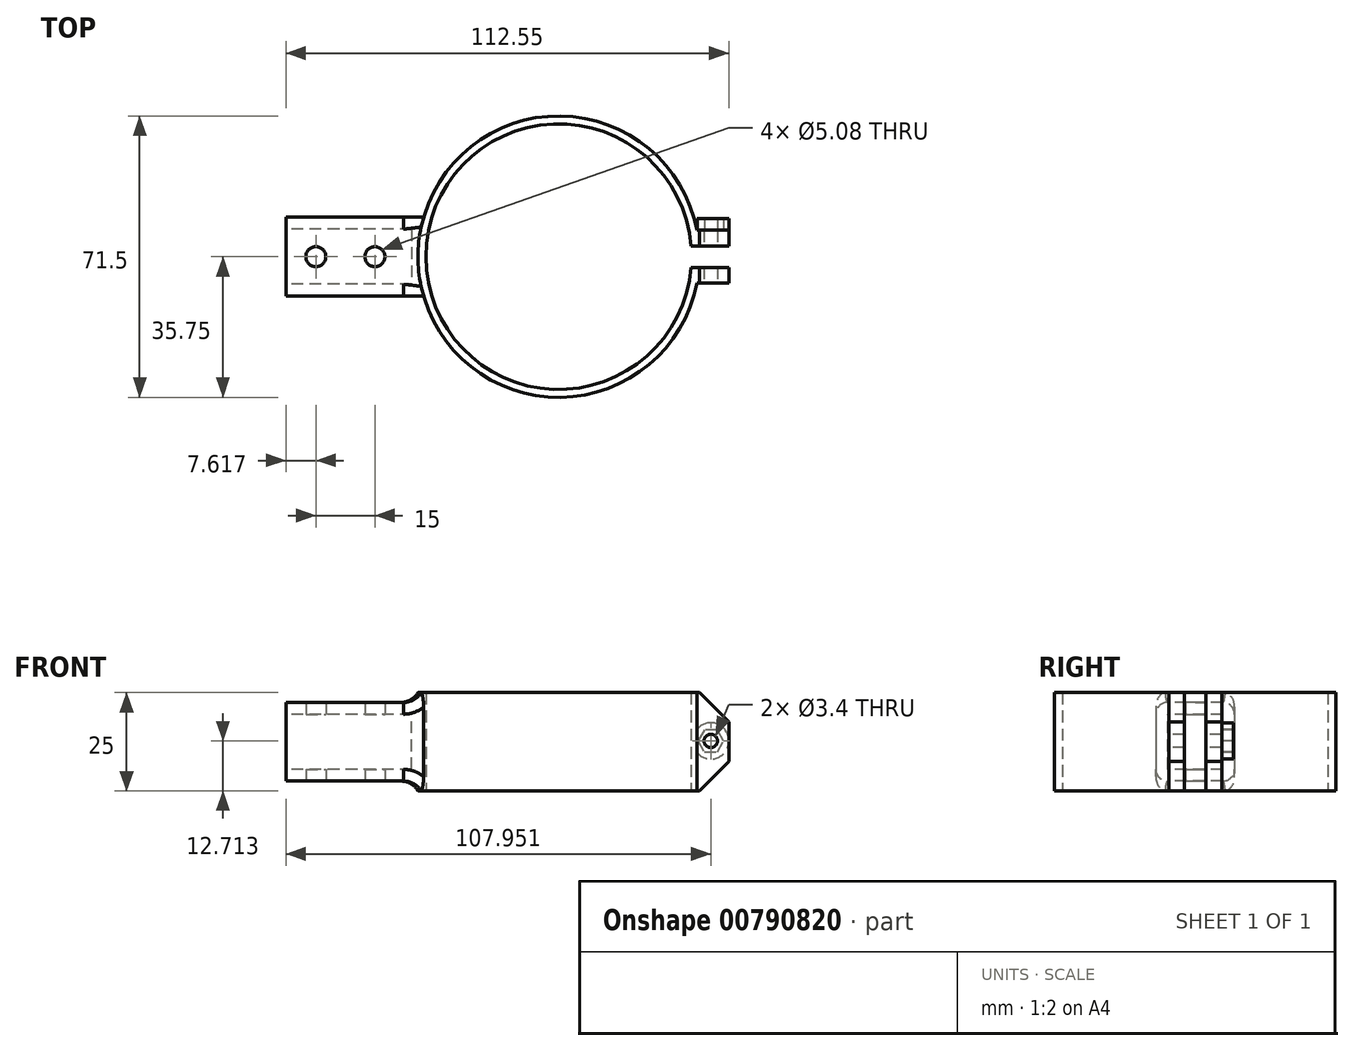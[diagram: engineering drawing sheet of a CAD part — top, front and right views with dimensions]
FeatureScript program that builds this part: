
annotation { "Feature Type Name" : "Feature", "Feature Type Description" : "" }
export const myFeature = defineFeature(function(context is Context, id is Id, definition is map)
    precondition{}
    {
        {
            var Q0;
            Q0=qCreatedBy(makeId("Top.planeOp"),FACE);
            var sketch = newSketch(context, id + "F0", { "sketchPlane" : qUnion([Q0])});
            skCircle(sketch, "E0", {"center": v(0, 0) * mm, "radius": 33.75 * mm});
            skCircle(sketch, "E1.0", {"center": v(0, 0) * mm, "radius": 35.75 * mm});
            skLineSegment(sketch, "E2.bottom", {"start": v(33.64, 6.72) * mm, "end": v(43.23, 6.72) * mm});
            skLineSegment(sketch, "E2.top", {"start": v(33.64, 2.72) * mm, "end": v(43.23, 2.72) * mm});
            skLineSegment(sketch, "E2.left", {"start": v(33.64, 6.72) * mm, "end": v(33.64, 2.72) * mm});
            skLineSegment(sketch, "E2.right", {"start": v(43.23, 6.72) * mm, "end": v(43.23, 2.72) * mm});
            skLineSegment(sketch, "E3.MirrorCS", {"start": v(33.64, -2.72) * mm, "end": v(43.23, -2.72) * mm});
            skLineSegment(sketch, "E4.MirrorCS", {"start": v(33.64, -6.72) * mm, "end": v(33.64, -2.72) * mm});
            skLineSegment(sketch, "E5.MirrorCS", {"start": v(43.23, -6.72) * mm, "end": v(43.23, -2.72) * mm});
            skLineSegment(sketch, "E6.MirrorCS", {"start": v(33.64, -6.72) * mm, "end": v(43.23, -6.72) * mm});
            skSolve(sketch);
        }
        {
            var Q0;
            {var subQ5=sQuery(id+"F0.wireOp",EDGE,"E2.right");Q0=makeQuery(id+"F0.imprint","IMPRINT",FACE,{"disambiguationData":[TD([[makeQuery(id+"F0.imprint","IMPRINT",EDGE,{"derivedFrom":subQ5}),-1.0]])]});}
            var Q1;
            {var subQ0=sQuery(id+"F0.wireOp",EDGE,"E2.left");Q1=makeQuery(id+"F0.imprint","IMPRINT",FACE,{"disambiguationData":[TD([[makeQuery(id+"F0.imprint","IMPRINT",EDGE,{"derivedFrom":subQ0}),-1.0]])]});}
            var Q2;
            {var subQ5=sQuery(id+"F0.wireOp",EDGE,"E2.left");Q2=makeQuery(id+"F0.imprint","IMPRINT",FACE,{"disambiguationData":[TD([[makeQuery(id+"F0.imprint","IMPRINT",EDGE,{"derivedFrom":subQ5}),1.0]])]});}
            var Q3;
            {var subQ5=sQuery(id+"F0.wireOp",EDGE,"E5.MirrorCS");Q3=makeQuery(id+"F0.imprint","IMPRINT",FACE,{"disambiguationData":[TD([[makeQuery(id+"F0.imprint","IMPRINT",EDGE,{"derivedFrom":subQ5}),1.0]])]});}
            var Q4;
            {var subQ5=sQuery(id+"F0.wireOp",EDGE,"E4.MirrorCS");Q4=makeQuery(id+"F0.imprint","IMPRINT",FACE,{"disambiguationData":[TD([[makeQuery(id+"F0.imprint","IMPRINT",EDGE,{"derivedFrom":subQ5}),-1.0]])]});}
            extrude(context, id + "F1", {"entities" : qUnion([Q0, Q1, Q2, Q3, Q4]), "depth" : 25 * mm, "offsetDistance" : 25 * mm});
        }
        {
            var Q0;
            Q0=makeQuery(id+"F1.opExtrude","CAP_EDGE",EDGE,{"disambiguationData":[OSD([sQuery(id+"F0.wireOp",EDGE,"E5.MirrorCS")])],"isStart":false});
            var Q1;
            Q1=makeQuery(id+"F1.opExtrude","CAP_EDGE",EDGE,{"disambiguationData":[OSD([sQuery(id+"F0.wireOp",EDGE,"E2.right")])],"isStart":false});
            var Q2;
            Q2=makeQuery(id+"F1.opExtrude","CAP_EDGE",EDGE,{"disambiguationData":[OSD([sQuery(id+"F0.wireOp",EDGE,"E5.MirrorCS")])],"isStart":true});
            var Q3;
            Q3=makeQuery(id+"F1.opExtrude","CAP_EDGE",EDGE,{"disambiguationData":[OSD([sQuery(id+"F0.wireOp",EDGE,"E2.right")])],"isStart":true});
            chamfer(context, id + "F2", {"entities" : qUnion([Q0, Q1, Q2, Q3]), "width" : 7.5 * mm, "tangentPropagation" : true});
        }
        {
            var Q0;
            Q0=makeQuery(id+"F1.opExtrude","SWEPT_FACE",FACE,{"disambiguationData":[OSD([sQuery(id+"F0.wireOp",EDGE,"E6.MirrorCS")])]});
            var sketch = newSketch(context, id + "F3", { "sketchPlane" : qUnion([Q0])});
            skCircle(sketch, "E7", {"center": v(38.63, 12.71) * mm, "radius": 1.7 * mm});
            skSolve(sketch);
        }
        {
            var Q0;
            Q0 = qSketchRegion(id + "F3", true);
            extrude(context, id + "F4", {"entities" : qUnion([Q0]), "operationType" : NewBodyOperationType.REMOVE, "oppositeDirection" : true, "depth" : 25 * mm, "offsetDistance" : 25 * mm});
        }
        {
            var Q0;
            Q0=makeQuery(id+"F1.opExtrude","SWEPT_FACE",FACE,{"disambiguationData":[OSD([sQuery(id+"F0.wireOp",EDGE,"E2.bottom")])]});
            var sketch = newSketch(context, id + "F5", { "sketchPlane" : qUnion([Q0])});
            skCircle(sketch, "E8.cCircle", {"center": v(-38.63, 12.71) * mm, "radius": 2.85 * mm, "construction": true});
            skLineSegment(sketch, "E8.0", {"start": v(-36.99, 9.86) * mm, "end": v(-40.28, 9.86) * mm});
            skLineSegment(sketch, "E8.1", {"start": v(-40.28, 9.86) * mm, "end": v(-41.92, 12.71) * mm});
            skLineSegment(sketch, "E8.2", {"start": v(-41.92, 12.71) * mm, "end": v(-40.28, 15.56) * mm});
            skLineSegment(sketch, "E8.3", {"start": v(-40.28, 15.56) * mm, "end": v(-36.99, 15.56) * mm});
            skLineSegment(sketch, "E8.4", {"start": v(-36.99, 15.56) * mm, "end": v(-35.34, 12.71) * mm});
            skLineSegment(sketch, "E8.5", {"start": v(-35.34, 12.71) * mm, "end": v(-36.99, 9.86) * mm});
            skPoint(sketch, "E8.0.midPoint", {"position": v(-38.63, 9.86) * mm});
            skCircle(sketch, "E9", {"center": v(-38.63, 12.71) * mm, "radius": 4.6 * mm});
            skSolve(sketch);
        }
        {
            var Q0;
            Q0=makeQuery(id+"F5.imprint","IMPRINT",FACE,{"disambiguationData":[TD([[makeQuery(id+"F5.imprint","IMPRINT",EDGE,{"derivedFrom":sQuery(id+"F5.wireOp",EDGE,"E8.0")}),1.0]])]});
            extrude(context, id + "F6", {"entities" : qUnion([Q0]), "operationType" : NewBodyOperationType.ADD, "depth" : 3 * mm, "offsetDistance" : 25 * mm});
        }
        {
            var Q0;
            Q0=qCreatedBy(makeId("Top.planeOp"),FACE);
            cPlane(context, id + "F7", {"entities" : qUnion([Q0]), "cplaneType" : CPlaneType.OFFSET, "offset" : 12.5 * mm, "width" : 150 * mm, "height" : 150 * mm});
        }
        {
            var Q0;
            Q0=qCreatedBy(id+"F7.planeOp",FACE);
            var sketch = newSketch(context, id + "F8", { "sketchPlane" : qUnion([Q0])});
            skLineSegment(sketch, "E10", {"start": v(-34.32, 10) * mm, "end": v(-69.32, 10) * mm});
            skLineSegment(sketch, "E11", {"start": v(-69.32, 10) * mm, "end": v(-69.32, -10) * mm});
            skLineSegment(sketch, "E12", {"start": v(-69.32, -10) * mm, "end": v(-34.32, -10) * mm});
            skLineSegment(sketch, "E13", {"start": v(-34.32, 10) * mm, "end": v(-33.75, 0) * mm});
            skLineSegment(sketch, "E14", {"start": v(-33.75, 0) * mm, "end": v(-34.32, -10) * mm});
            skSolve(sketch);
        }
        {
            var Q0;
            Q0 = qSketchRegion(id + "F8", true);
            extrude(context, id + "F9", {"entities" : qUnion([Q0]), "operationType" : NewBodyOperationType.ADD, "depth" : 10 * mm, "offsetDistance" : 25 * mm, "hasSecondDirection" : true, "secondDirectionOppositeDirection" : true, "secondDirectionDepth" : 10 * mm});
        }
        {
            var Q0;
            Q0=makeQuery(id+"F9.opExtrude","SWEPT_FACE",FACE,{"disambiguationData":[OSD([sQuery(id+"F8.wireOp",EDGE,"E11")])]});
            var sketch = newSketch(context, id + "F10", { "sketchPlane" : qUnion([Q0])});
            skSolve(sketch);
        }
        {
            var Q0;
            {var subQ0=sQuery(id+"F8.wireOp",EDGE,"E11");Q0=makeQuery(id+"F10.imprint","IMPRINT",FACE,{"disambiguationData":[TD([[makeQuery(id+"F10.imprint","IMPRINT",EDGE,{"derivedFrom":makeQuery(id+"F9.opExtrude","CAP_EDGE",EDGE,{"disambiguationData":[OSD([subQ0])],"isStart":true})}),1.0]])]});}
            var sketch = newSketch(context, id + "F11", { "sketchPlane" : qUnion([Q0])});
            skLineSegment(sketch, "E15.bottom", {"start": v(-7, 5.5) * mm, "end": v(7, 5.5) * mm});
            skLineSegment(sketch, "E15.top", {"start": v(-7, 19.5) * mm, "end": v(7, 19.5) * mm});
            skLineSegment(sketch, "E15.left", {"start": v(-7, 5.5) * mm, "end": v(-7, 19.5) * mm});
            skLineSegment(sketch, "E15.right", {"start": v(7, 5.5) * mm, "end": v(7, 19.5) * mm});
            skSolve(sketch);
        }
        {
            var Q0;
            Q0 = qSketchRegion(id + "F11", true);
            extrude(context, id + "F12", {"entities" : qUnion([Q0]), "operationType" : NewBodyOperationType.REMOVE, "oppositeDirection" : true, "depth" : 32 * mm, "offsetDistance" : 25 * mm});
        }
        {
            var Q0;
            Q0=makeQuery(id+"F9.opExtrude","CAP_FACE",FACE,{"disambiguationData":[OSD([sQuery(id+"F8.wireOp",EDGE,"E10"),sQuery(id+"F8.wireOp",EDGE,"E11"),sQuery(id+"F8.wireOp",EDGE,"E12"),sQuery(id+"F8.wireOp",EDGE,"E13"),sQuery(id+"F8.wireOp",EDGE,"E14")])],"isStart":true});
            var sketch = newSketch(context, id + "F13", { "sketchPlane" : qUnion([Q0])});
            skCircle(sketch, "E16", {"center": v(-61.7, 0) * mm, "radius": 2.54 * mm});
            skLineSegment(sketch, "E17", {"start": v(-61.7, 0) * mm, "end": v(-69.32, 0) * mm, "construction": true});
            skLineSegment(sketch, "E18", {"start": v(-61.7, 0) * mm, "end": v(-46.7, 0) * mm, "construction": true});
            skCircle(sketch, "E19", {"center": v(-46.7, 0) * mm, "radius": 2.54 * mm});
            skSolve(sketch);
        }
        {
            var Q0;
            Q0=makeQuery(id+"F13.imprint","IMPRINT",FACE,{"disambiguationData":[TD([[makeQuery(id+"F13.imprint","IMPRINT",EDGE,{"derivedFrom":sQuery(id+"F13.wireOp",EDGE,"E16")}),1.0]])]});
            extrude(context, id + "F14", {"entities" : qUnion([Q0]), "operationType" : NewBodyOperationType.REMOVE, "oppositeDirection" : true, "depth" : 25 * mm, "offsetDistance" : 25 * mm});
        }
        {
            var Q0;
            Q0=makeQuery(id+"F9.opExtrude","SWEPT_EDGE",EDGE,{"disambiguationData":[OSD([sQuery(id+"F8.wireOp",EDGE,"E12"),sQuery(id+"F8.wireOp",EDGE,"E14")])]});
            var Q1;
            Q1=makeQuery(id+"F9.boolean.opBoolean","INTERSECT",EDGE,{"derivedFrom":[makeQuery(id+"F1.opExtrude","SWEPT_FACE",FACE,{"disambiguationData":[OSD([sQuery(id+"F0.wireOp",EDGE,"E1.0")])]}),makeQuery(id+"F9.opExtrude","CAP_FACE",FACE,{"disambiguationData":[OSD([sQuery(id+"F8.wireOp",EDGE,"E10"),sQuery(id+"F8.wireOp",EDGE,"E11"),sQuery(id+"F8.wireOp",EDGE,"E12"),sQuery(id+"F8.wireOp",EDGE,"E13"),sQuery(id+"F8.wireOp",EDGE,"E14")])],"isStart":false})]});
            var Q2;
            Q2=makeQuery(id+"F9.boolean.opBoolean","INTERSECT",EDGE,{"derivedFrom":[makeQuery(id+"F1.opExtrude","SWEPT_FACE",FACE,{"disambiguationData":[OSD([sQuery(id+"F0.wireOp",EDGE,"E1.0")])]}),makeQuery(id+"F9.opExtrude","CAP_FACE",FACE,{"disambiguationData":[OSD([sQuery(id+"F8.wireOp",EDGE,"E10"),sQuery(id+"F8.wireOp",EDGE,"E11"),sQuery(id+"F8.wireOp",EDGE,"E12"),sQuery(id+"F8.wireOp",EDGE,"E13"),sQuery(id+"F8.wireOp",EDGE,"E14")])],"isStart":true})]});
            var Q3;
            Q3=makeQuery(id+"F9.opExtrude","SWEPT_EDGE",EDGE,{"disambiguationData":[OSD([sQuery(id+"F8.wireOp",EDGE,"E10"),sQuery(id+"F8.wireOp",EDGE,"E13")])]});
            fillet(context, id + "F15", {"entities" : qUnion([Q0, Q1, Q2, Q3]), "radius" : 5 * mm, "tangentPropagation" : true, "allowEdgeOverflow" : false});
        }
        {
            var Q0;
            Q0=makeQuery(id+"F9.opExtrude","CAP_EDGE",EDGE,{"disambiguationData":[OSD([sQuery(id+"F8.wireOp",EDGE,"E12")])],"isStart":true});
            var Q1;
            Q1=makeQuery(id+"F9.opExtrude","CAP_EDGE",EDGE,{"disambiguationData":[OSD([sQuery(id+"F8.wireOp",EDGE,"E10")])],"isStart":true});
            var Q2;
            Q2=makeQuery(id+"F9.opExtrude","CAP_EDGE",EDGE,{"disambiguationData":[OSD([sQuery(id+"F8.wireOp",EDGE,"E10")])],"isStart":false});
            var Q3;
            Q3=makeQuery(id+"F9.opExtrude","CAP_EDGE",EDGE,{"disambiguationData":[OSD([sQuery(id+"F8.wireOp",EDGE,"E12")])],"isStart":false});
            fillet(context, id + "F16", {"entities" : qUnion([Q0, Q1, Q2, Q3]), "radius" : 3 * mm, "tangentPropagation" : true, "allowEdgeOverflow" : false});
        }
        {
            var Q0;
            Q0=makeQuery(id+"F13.imprint","IMPRINT",FACE,{"disambiguationData":[TD([[makeQuery(id+"F13.imprint","IMPRINT",EDGE,{"derivedFrom":sQuery(id+"F13.wireOp",EDGE,"E19")}),1.0]])]});
            extrude(context, id + "F17", {"entities" : qUnion([Q0]), "operationType" : NewBodyOperationType.REMOVE, "oppositeDirection" : true, "depth" : 25 * mm, "offsetDistance" : 25 * mm});
        }
    });
